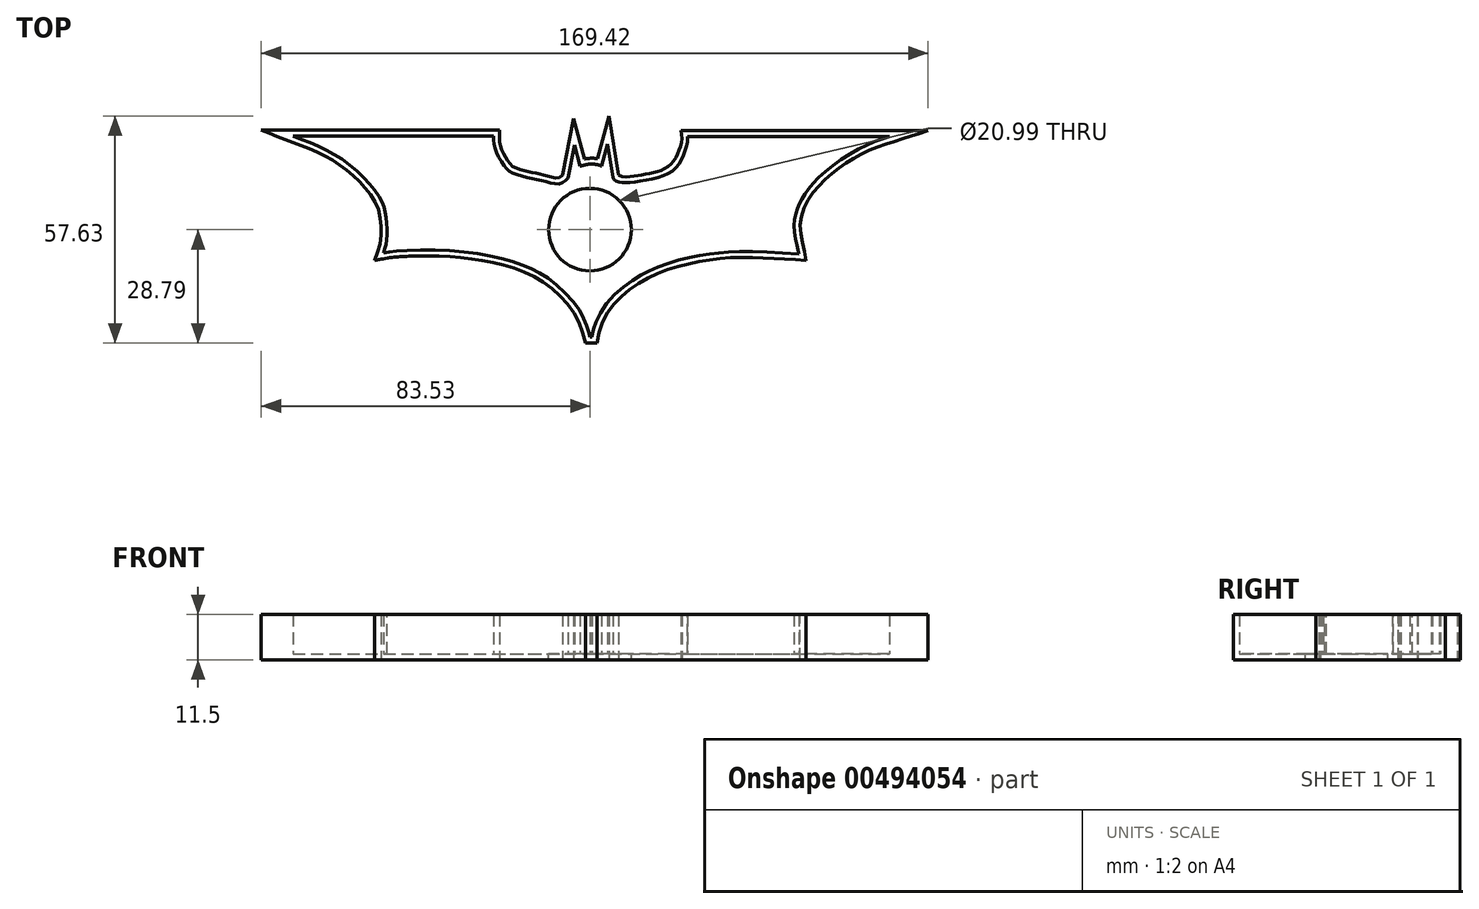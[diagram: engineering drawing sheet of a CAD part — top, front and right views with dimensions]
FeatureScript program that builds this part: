
annotation { "Feature Type Name" : "Feature", "Feature Type Description" : "" }
export const myFeature = defineFeature(function(context is Context, id is Id, definition is map)
    precondition{}
    {
        {
            var Q0;
            Q0=qCreatedBy(makeId("Top.planeOp"),FACE);
            var sketch = newSketch(context, id + "F0", { "sketchPlane" : qUnion([Q0])});
            skLineSegment(sketch, "E0", {"start": v(-75.38, 23.76) * mm, "end": v(-25, 23.76) * mm});
            skLineSegment(sketch, "E1", {"start": v(24.8, 23.6) * mm, "end": v(76.1, 23.6) * mm});
            skFitSpline(sketch, "E2", {"points": [v(-75.38, 23.76) * mm, v(-62.52, 17.55) * mm, v(-53.44, 8.17) * mm, v(-51.78, 3.03) * mm, v(-51.63, -2.57) * mm, v(-52.49, -5.89) * mm], "startDerivative": vector(48.82, -18.6) * mm, "endDerivative": vector(-7.89, -22.83) * mm});
            skFitSpline(sketch, "E3", {"points": [v(-52.49, -5.89) * mm, v(-49.39, -5.46) * mm, v(-36.76, -5.3) * mm, v(-23.54, -7.07) * mm, v(-15.63, -9.63) * mm, v(-9.47, -13.22) * mm, v(-2.9, -20.18) * mm, v(-0.7, -24.88) * mm, v(0, -27.3) * mm], "startDerivative": vector(30.91, 5.52) * mm, "endDerivative": vector(8.26, -30.54) * mm});
            skFitSpline(sketch, "E4", {"points": [v(0, -27.3) * mm, v(0.48, -27.3) * mm], "startDerivative": vector(0.48, 0) * mm, "endDerivative": vector(0.48, 0) * mm});
            skFitSpline(sketch, "E5", {"points": [v(0.48, -27.3) * mm, v(0.6, -26.54) * mm, v(1.07, -24.76) * mm, v(4.1, -18.9) * mm, v(10.97, -12.8) * mm, v(16.37, -9.87) * mm, v(23.94, -7.4) * mm, v(31.07, -6.12) * mm, v(37.94, -5.55) * mm, v(53.09, -6.18) * mm], "startDerivative": vector(2.97, 17.96) * mm, "endDerivative": vector(95.82, -6.04) * mm});
            skFitSpline(sketch, "E6", {"points": [v(76.1, 23.6) * mm, v(69.44, 21.11) * mm, v(60.4, 15.32) * mm, v(55.44, 10.23) * mm, v(53.47, 7.12) * mm, v(52.39, 4.32) * mm, v(51.88, 0.56) * mm, v(52.64, -4.02) * mm, v(53.09, -6.18) * mm], "startDerivative": vector(-42.57, -13.36) * mm, "endDerivative": vector(4.54, -23.2) * mm});
            skFitSpline(sketch, "E7", {"points": [v(24.8, 23.6) * mm, v(24.8, 22.36) * mm, v(23.73, 18.94) * mm, v(21.56, 15.43) * mm, v(17.24, 13.22) * mm, v(11.23, 12.12) * mm, v(8.25, 11.92) * mm, v(6.56, 12.36) * mm, v(5.8, 13.27) * mm], "startDerivative": vector(1.36, -13.64) * mm, "endDerivative": vector(-8.05, 12.98) * mm});
            skLineSegment(sketch, "E8", {"start": v(5.8, 13.27) * mm, "end": v(4.45, 21.73) * mm});
            skLineSegment(sketch, "E9", {"start": v(4.45, 21.73) * mm, "end": v(2.91, 16.1) * mm});
            skFitSpline(sketch, "E10", {"points": [v(2.91, 16.1) * mm, v(1.9, 16.5) * mm, v(0.46, 16.63) * mm, v(-1.08, 16.5) * mm, v(-2.47, 16.1) * mm], "startDerivative": vector(-4.3, 1.97) * mm, "endDerivative": vector(-5.35, -1.7) * mm});
            skLineSegment(sketch, "E11", {"start": v(-2.47, 16.1) * mm, "end": v(-3.92, 21.5) * mm});
            skLineSegment(sketch, "E12", {"start": v(-5.55, 13.08) * mm, "end": v(-3.92, 21.5) * mm});
            skFitSpline(sketch, "E13", {"points": [v(-25, 23.76) * mm, v(-24.5, 23.76) * mm], "startDerivative": vector(0.5, 0) * mm, "endDerivative": vector(0.5, 0) * mm});
            skFitSpline(sketch, "E14", {"points": [v(-24.5, 23.76) * mm, v(-24.16, 20.72) * mm, v(-22.04, 16.54) * mm, v(-19.93, 14.52) * mm, v(-15.45, 13.17) * mm, v(-11.18, 12.16) * mm, v(-7.57, 11.68) * mm, v(-5.55, 13.08) * mm], "startDerivative": vector(0.08, -21.97) * mm, "endDerivative": vector(15.33, 15.4) * mm});
            skSolve(sketch);
        }
        {
            var Q0;
            Q0=makeQuery(id+"F0.imprint","IMPRINT",FACE,{"disambiguationData":[TD([[makeQuery(id+"F0.imprint","IMPRINT",EDGE,{"derivedFrom":sQuery(id+"F0.wireOp",EDGE,"E0")}),-1.0]])]});
            extrude(context, id + "F1", {"entities" : qUnion([Q0]), "depth" : 10 * mm});
        }
        {
            var Q0;
            Q0=makeQuery(id+"F1.opExtrude","CAP_FACE",FACE,{"disambiguationData":[OSD([sQuery(id+"F0.wireOp",EDGE,"E0"),sQuery(id+"F0.wireOp",EDGE,"E1"),sQuery(id+"F0.wireOp",EDGE,"E2"),sQuery(id+"F0.wireOp",EDGE,"E3"),sQuery(id+"F0.wireOp",EDGE,"E4"),sQuery(id+"F0.wireOp",EDGE,"E5"),sQuery(id+"F0.wireOp",EDGE,"E6"),sQuery(id+"F0.wireOp",EDGE,"E7"),sQuery(id+"F0.wireOp",EDGE,"E8"),sQuery(id+"F0.wireOp",EDGE,"E9"),sQuery(id+"F0.wireOp",EDGE,"E10"),sQuery(id+"F0.wireOp",EDGE,"E11"),sQuery(id+"F0.wireOp",EDGE,"E12"),sQuery(id+"F0.wireOp",EDGE,"E13"),sQuery(id+"F0.wireOp",EDGE,"E14")])],"isStart":false});
            shell(context, id + "F2", {"entities" : qUnion([Q0]), "thickness" : 1.5 * mm, "oppositeDirection" : true});
        }
        {
            var Q0;
            Q0=qCreatedBy(makeId("Top.planeOp"),FACE);
            var sketch = newSketch(context, id + "F3", { "sketchPlane" : qUnion([Q0])});
            skCircle(sketch, "E15", {"center": v(0, 0) * mm, "radius": 10.5 * mm});
            skSolve(sketch);
        }
        {
            var Q0;
            Q0 = qSketchRegion(id + "F3", true);
            extrude(context, id + "F4", {"entities" : qUnion([Q0]), "operationType" : NewBodyOperationType.REMOVE, "oppositeDirection" : true, "depth" : 25 * mm});
        }
    });
